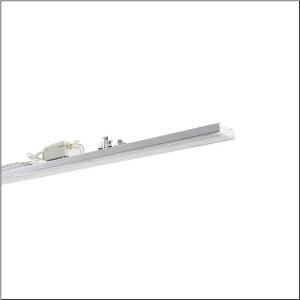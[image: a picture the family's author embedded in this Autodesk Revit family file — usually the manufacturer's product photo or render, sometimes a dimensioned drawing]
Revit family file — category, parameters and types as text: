
# Revit family: licross_r__21_recessed_mo_52tl14mn4axg_742d
name_source: partatom
category: Lighting Fixtures
units: mm (PartAtom-declared; Revit-internal decimal feet)

## family parameters
Cut with Voids When Loaded = No
Host = Face
Light Source = No
Part Type = Normal
Room Calculation Point = No
Round Connector Dimension = Use Diameter
Shared = No

## types (1)
- --- (1 x LED, 10120 lm, 60.5 W, 4000K)
    Apparent Load = 61 VA
    CIE Flux Codes = 56 84 97 100 100
    Color Rendering = 80
    Color Temperature = 4000K
    Default Elevation = 1800 mm
    Description = Licross® 21 Recessed MO, luminaire insert, of sheet steel, galvanised, coil coated, white, length: 1.500mm, width: 66mm, height: 67mm, LED rated luminous flux: 10.120lm, light colour: 840, control gear: ON/OFF Multilumen, with plug, 3-pole, with phase selection, mains connection: 220..240V, AC, 50/60Hz, rated input power: 61W, halogen-free wiring, primary light control with lens, of plastic, primary optical cover: cover, of PMMA, light emission: direct distribution, primary light characteristic: asymmetric, protection rating (complete): IP40, insulation class (complete): insulation class I (protective earthing), certification: CE, ENEC, VDE, UKCA, protection symbol: D if used in an environment without relevant dust loads with corresponding accessories, impact resistance: IK06, permissible ambient temperature for indoor applications: -35..+40°C, corresponds to IFS (International Featured Standards) requirements for safety and quality in the food industry, reducing of maximum allowable ambient temperature of 5°C with ceiling mounting, LABS conformity tested according to VDMA 24364:2018-05, packaging unit: 1 piece
    Height = 58 mm
    Lamp = 1 x LED
    Lamp Light Flux = 10120 lm
    Lamp Power = 60.5 W
    Lamp count = 1
    Length = 1500 mm
    Luminous efficacy = 167 lm/W
    Manufacturer = Siteco
    ModVariant = No
    Model = 52TL14MN4AXG
    Mounting Place = Ceiling
    Mounting Type = Pendant
    Number of Poles = 1
    OnlyDefault = Yes
    Power Factor = 1
    Product Name = Licross® 21 Recessed MO
    Product group = luminaire insert
    ProductGroupID = 901
    Protection Class = Protection class I
    Protection Degree = IP 40
    RLX_Detail_Level = 1
    RLX_Emergency_Light_Flux = 0 lm
    RLX_Emergency_Type = 0
    RLX_Emergency_Type_DB = No
    RlxData = <blob elided: 22733 chars, md5=49bced84>
    Socket = socket
    Standby Power = 0 W
    System Light Flux = 10120 lm
    System Power = 61 W
    Type Comments = factory setting: luminous flux: 100 % | (A | C | E) | 140 mA
    Type Image = l_1296930.jpg
    URL = http://relux.com
    VarID = @adj_038225
    Voltage = 0 V
    Weight = 0.00 kg
    Width = 66 mm

## geometry (parser evidence)
native form markers: Blend x4, Sweep x11
no freeform markers — native parametric forms only
